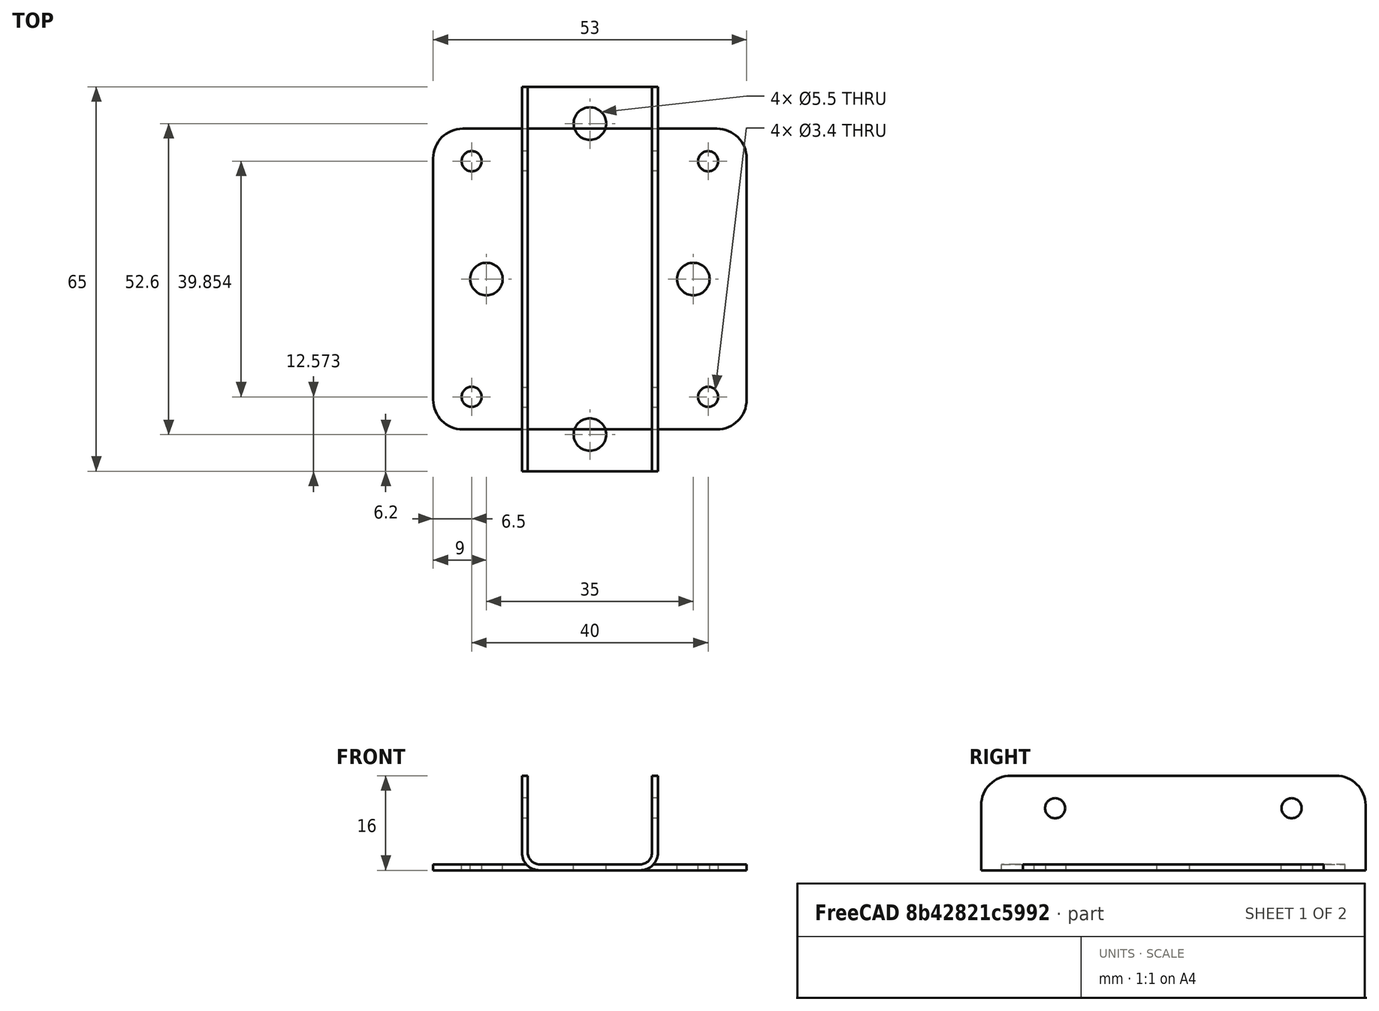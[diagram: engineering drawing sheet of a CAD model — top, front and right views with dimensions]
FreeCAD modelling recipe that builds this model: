
FCSTD DOCUMENT  (FreeCAD 1.1R38827 (Git))
Label: U-fix
License: All rights reserved
LicenseURL: http://en.wikipedia.org/wiki/All_rights_reserved
objects: Sketcher::SketchObject×7, TechDraw::DrawViewDimension×4, TechDraw::DrawViewPart×3, PartDesign::SubShapeBinder×2, PartDesign::Pocket×2, PartDesign::FeaturePython×1, PartDesign::Mirrored×1, TechDraw::DrawSVGTemplate×1, Part::Feature×1, PartDesign::Hole×1, PartDesign::Body×1, TechDraw::DrawPage×1, App::DocumentObjectGroup×1
note: 37 computed .brp shape members not serialized (recipe doc carries the construction recipe); baked Part::Feature solids carry a one-line shape summary decoded from their .brp
EXTERNAL_REF file=ugol90degX40mm.FCStd obj=Binder002
EXTERNAL_REF file=wheel50mm.FCStd obj=Populate001

FEATURE [Sketcher::SketchObject] Sketch
  ArcFitTolerance = 0
  AttachmentSupport = -> [XZ_Plane]
  FullyConstrained = true
  MakeInternals = false
  MapMode = 5
  Placement = pos=(0,0,0) rot=(1,0,0;1.5708rad)
  sketch-geometry (5):
    g0: LineSegment StartX=-11.5 StartY=16 StartZ=0 EndX=-11.5 EndY=0 EndZ=0
    g1: LineSegment StartX=-11.5 StartY=0 StartZ=0 EndX=11.5 EndY=0 EndZ=0
    g2: LineSegment StartX=11.5 StartY=0 StartZ=0 EndX=11.5 EndY=16 EndZ=0
    g3: LineSegment [constr] StartX=11.5 StartY=16 StartZ=0 EndX=-11.5 EndY=16 EndZ=0
    g4: GeomPoint [constr] X=0 Y=8 Z=0
  constraints (13):
    c: Coincident(g0,g1)
    c: Coincident(g1,g2)
    c: Coincident(g2,g3)
    c: Coincident(g3,g0)
    c: Horizontal(g1)
    c: Horizontal(g3)
    c: Vertical(g0)
    c: Vertical(g2)
    c: Symmetric(g1,g0,g4)
    c: PointOnObject(g4,g-2)
    c: PointOnObject(g1,g-1)
    c: DistanceX(g1,g1) = 23  'width'
    c: DistanceY(g2) = 16  'height'
FEATURE [PartDesign::FeaturePython] BaseBend  # WARN: FeaturePython — macro-defined, semantics opaque (R4)
  BendSide = 1
  BendSketch = -> Sketch
  MidPlane = true
  Reverse = false
  Suppressed = false
  length = 65
  radius = 2
  thickness = 1
FEATURE [PartDesign::SubShapeBinder] Binder  label="U-fix_vert_holes"
  BindCopyOnChange = 0
  BindMode = 0
  ClaimChildren = false
  Context = -> Body [Binder.]
  Fuse = false
  MakeFace = true
  OffsetFill = false
  OffsetIntersection = false
  OffsetJoinType = 0
  OffsetOpenResult = false
  PartialLoad = false
  Placement = pos=(0,0,0) rot=(0,0,1;1.5708rad)
  Relative = true
  Support = -> [<external ugol90degX40mm.FCStd>#Binder002]
  _Version = 2
  expr: Support = <<ugol90degX40mm>>#<<vert>>._self
FEATURE [PartDesign::Pocket] Pocket
  BaseFeature = -> BaseBend
  Direction = (1,-2e-16,0)
  Length = 5
  Length2 = 5
  Midplane = true
  Profile = -> Binder
  Suppressed = false
  Type = 1
FEATURE [Sketcher::SketchObject] Sketch001
  ArcFitTolerance = 0
  AttachmentOffset = pos=(32.5,16,0) rot=(0,0,1;0rad)
  AttachmentSupport = -> [YZ_Plane]
  FullyConstrained = true
  MakeInternals = false
  MapMode = 5
  Placement = pos=(0,32.5,16) rot=(0.57735,0.57735,0.57735;2.0944rad)
  expr: .AttachmentOffset.Base.x = BaseBend.length / 2
  expr: .AttachmentOffset.Base.y = Sketch.Constraints.height
  sketch-geometry (3):
    g0: ArcOfCircle CenterX=-5 CenterY=-5 CenterZ=0 NormalX=0 NormalY=0 NormalZ=1 AngleXU=0 Radius=5 StartAngle=0 EndAngle=1.5708
    g1: LineSegment StartX=-9e-16 StartY=-5 StartZ=0 EndX=0 EndY=0 EndZ=0
    g2: LineSegment StartX=0 StartY=0 StartZ=0 EndX=-5.00003 EndY=-4.65468e-11 EndZ=0
  constraints (8):
    c: PointOnObject(g0,g-1)
    c: PointOnObject(g0,g-2)
    c: Coincident(g1,g2)
    c: Coincident(g2,g0)
    c: Tangent(g2,g0)
    c: Tangent(g0,g1) = -1.5708
    c: Coincident(g1,g-1)
    c: Diameter(g0) = 10
FEATURE [PartDesign::Pocket] Pocket001
  BaseFeature = -> Pocket
  Direction = (-1,0,0)
  Length = 5
  Length2 = 5
  Midplane = true
  Profile = -> Sketch001
  ReferenceAxis = -> Sketch001 [N_Axis]
  Suppressed = false
  Type = 1
FEATURE [PartDesign::Mirrored] Mirrored
  BaseFeature = -> Pocket001
  MirrorPlane = -> XZ_Plane
  Originals = -> [Pocket001]
  Suppressed = false
  TransformMode = 0
FEATURE [Sketcher::SketchObject] Sketch002  label="holes_bottom"
  ArcFitTolerance = 0
  AttachmentSupport = -> [XY_Plane]
  FullyConstrained = true
  MakeInternals = false
  MapMode = 5
  sketch-geometry (2):
    g0: Circle CenterX=0 CenterY=17.5 CenterZ=0 NormalX=0 NormalY=0 NormalZ=1 AngleXU=0 Radius=2.5
    g1: Circle CenterX=0 CenterY=-17.5 CenterZ=0 NormalX=0 NormalY=0 NormalZ=1 AngleXU=0 Radius=2.5
  constraints (5):
    c: PointOnObject(g0,g-2)
    c: Symmetric(g1,g0,g-1)
    c: Equal(g1,g0)
    c: Diameter(g1) = 5
    c: DistanceY(g1,g0) = 35
FEATURE [TechDraw::DrawSVGTemplate] Template
  Height = 210
  Orientation = 1
  Template = <path>
  Width = 297
FEATURE [Part::Feature] Unfold
  Placement = pos=(0,0,0) rot=(0,0,1;1.5708rad)
  shape: bbox 53 x 50.85 x 1 mm, 16 faces (baked)
FEATURE [Sketcher::SketchObject] Unfold_Sketch_Outline
  ArcFitTolerance = 0
  FullyConstrained = false
  MakeInternals = false
  sketch-geometry (8):
    g0: ArcOfCircle CenterX=21.5 CenterY=-20.427 CenterZ=0 NormalX=0 NormalY=0 NormalZ=1 AngleXU=4e-16 Radius=5 StartAngle=4.71238 EndAngle=6.28319
    g1: LineSegment StartX=26.5 StartY=20.427 StartZ=0 EndX=26.5 EndY=-20.427 EndZ=0
    g2: ArcOfCircle CenterX=21.5 CenterY=20.427 CenterZ=0 NormalX=0 NormalY=0 NormalZ=1 AngleXU=-4e-16 Radius=5 StartAngle=0 EndAngle=1.5708
    g3: LineSegment StartX=21.5 StartY=25.427 StartZ=0 EndX=-21.5 EndY=25.427 EndZ=0
    g4: ArcOfCircle CenterX=-21.5 CenterY=20.427 CenterZ=0 NormalX=0 NormalY=0 NormalZ=1 AngleXU=-3.14159 Radius=5 StartAngle=4.71238 EndAngle=6.28319
    g5: LineSegment StartX=-26.5 StartY=20.427 StartZ=0 EndX=-26.5 EndY=-20.427 EndZ=0
    g6: ArcOfCircle CenterX=-21.5 CenterY=-20.427 CenterZ=0 NormalX=0 NormalY=0 NormalZ=1 AngleXU=3.14159 Radius=5 StartAngle=0 EndAngle=1.5708
    g7: LineSegment StartX=21.5 StartY=-25.427 StartZ=0 EndX=-21.5 EndY=-25.427 EndZ=0
FEATURE [Sketcher::SketchObject] Unfold_Sketch_Internal
  ArcFitTolerance = 0
  FullyConstrained = false
  MakeInternals = false
  sketch-geometry (6):
    g0: Circle CenterX=17.5 CenterY=0 CenterZ=0 NormalX=0 NormalY=0 NormalZ=1 AngleXU=1.5708 Radius=2.75
    g1: Circle CenterX=-17.5 CenterY=0 CenterZ=0 NormalX=0 NormalY=0 NormalZ=1 AngleXU=1.5708 Radius=2.75
    g2: Circle CenterX=20 CenterY=-19.927 CenterZ=0 NormalX=0 NormalY=0 NormalZ=1 AngleXU=2e-16 Radius=1.7
    g3: Circle CenterX=-20 CenterY=-19.927 CenterZ=0 NormalX=0 NormalY=0 NormalZ=1 AngleXU=2e-16 Radius=1.7
    g4: Circle CenterX=20 CenterY=19.927 CenterZ=0 NormalX=0 NormalY=0 NormalZ=-1 AngleXU=-3.14159 Radius=1.7
    g5: Circle CenterX=-20 CenterY=19.927 CenterZ=0 NormalX=0 NormalY=0 NormalZ=-1 AngleXU=-3.14159 Radius=1.7
FEATURE [Sketcher::SketchObject] Unfold_Sketch_bends
  ArcFitTolerance = 0
  FullyConstrained = false
  MakeInternals = false
  sketch-geometry (2):
    g0: LineSegment StartX=-26.5 StartY=10.4635 StartZ=0 EndX=26.5 EndY=10.4635 EndZ=0
    g1: LineSegment StartX=-26.5 StartY=-10.4635 StartZ=0 EndX=26.5 EndY=-10.4635 EndZ=0
FEATURE [Sketcher::SketchObject] Unfold_Sketch
  ArcFitTolerance = 0
  ExternalGeometry = -> [Unfold_Sketch_bends]
  FullyConstrained = false
  MakeInternals = false
  sketch-geometry (18):
    g0: ArcOfCircle CenterX=21.5 CenterY=-20.427 CenterZ=0 NormalX=0 NormalY=0 NormalZ=1 AngleXU=4e-16 Radius=5 StartAngle=4.71238 EndAngle=6.28319
    g1: LineSegment StartX=21.5 StartY=-25.427 StartZ=0 EndX=-21.5 EndY=-25.427 EndZ=0
    g2: ArcOfCircle CenterX=-21.5 CenterY=-20.427 CenterZ=0 NormalX=0 NormalY=0 NormalZ=1 AngleXU=3.14159 Radius=5 StartAngle=0 EndAngle=1.5708
    g3: ArcOfCircle CenterX=-21.5 CenterY=20.427 CenterZ=0 NormalX=0 NormalY=0 NormalZ=1 AngleXU=-3.14159 Radius=5 StartAngle=4.71238 EndAngle=6.28319
    g4: LineSegment StartX=21.5 StartY=25.427 StartZ=0 EndX=-21.5 EndY=25.427 EndZ=0
    g5: ArcOfCircle CenterX=21.5 CenterY=20.427 CenterZ=0 NormalX=0 NormalY=0 NormalZ=1 AngleXU=-4e-16 Radius=5 StartAngle=0 EndAngle=1.5708
    g6: Circle CenterX=-17.5 CenterY=0 CenterZ=0 NormalX=0 NormalY=0 NormalZ=1 AngleXU=1.5708 Radius=2.75
    g7: Circle CenterX=17.5 CenterY=0 CenterZ=0 NormalX=0 NormalY=0 NormalZ=1 AngleXU=1.5708 Radius=2.75
    g8: Circle CenterX=-20 CenterY=19.927 CenterZ=0 NormalX=0 NormalY=0 NormalZ=-1 AngleXU=-3.14159 Radius=1.7
    g9: Circle CenterX=20 CenterY=19.927 CenterZ=0 NormalX=0 NormalY=0 NormalZ=-1 AngleXU=-3.14159 Radius=1.7
    g10: Circle CenterX=-20 CenterY=-19.927 CenterZ=0 NormalX=0 NormalY=0 NormalZ=1 AngleXU=2e-16 Radius=1.7
    g11: Circle CenterX=20 CenterY=-19.927 CenterZ=0 NormalX=0 NormalY=0 NormalZ=1 AngleXU=2e-16 Radius=1.7
    g12: LineSegment StartX=26.5 StartY=20.427 StartZ=0 EndX=26.5 EndY=-20.427 EndZ=0
    g13: LineSegment StartX=-26.5 StartY=20.427 StartZ=0 EndX=-26.5 EndY=-20.427 EndZ=0
    g14: LineSegment StartX=26.5 StartY=-10.4635 StartZ=0 EndX=24.5 EndY=-10.4635 EndZ=0
    g15: LineSegment StartX=26.5 StartY=10.4635 StartZ=0 EndX=24.5 EndY=10.4635 EndZ=0
    g16: LineSegment StartX=-26.5 StartY=10.4635 StartZ=0 EndX=-24.5 EndY=10.4635 EndZ=0
    g17: LineSegment StartX=-26.5 StartY=-10.4635 StartZ=0 EndX=-24.5 EndY=-10.4635 EndZ=0
  constraints (20):
    c: Coincident(g2,g13)
    c: Coincident(g3,g13)
    c: Coincident(g1,g2)
    c: Coincident(g3,g4)
    c: Coincident(g0,g1)
    c: Coincident(g4,g5)
    c: Coincident(g0,g12)
    c: Coincident(g5,g12)
    c: Coincident(g14,g-4)
    c: Coincident(g15,g-3)
    c: Coincident(g16,g-3)
    c: Coincident(g17,g-4)
    c: PointOnObject(g17,g-4)
    c: PointOnObject(g16,g-3)
    c: PointOnObject(g15,g-3)
    c: PointOnObject(g14,g-4)
    c: Equal(g14,g15)
    c: Equal(g15,g16)
    c: Equal(g16,g17)
    c: Distance(g17) = 2
FEATURE [PartDesign::SubShapeBinder] Binder001
  BindCopyOnChange = 0
  BindMode = 0
  ClaimChildren = false
  Context = -> Body [Binder001.]
  Fuse = false
  MakeFace = true
  OffsetFill = false
  OffsetIntersection = false
  OffsetJoinType = 0
  OffsetOpenResult = false
  PartialLoad = false
  Placement = pos=(0,0,0) rot=(0,0,1;0.785398rad)
  Relative = true
  Support = -> [<external wheel50mm.FCStd>#Populate001]
  _Version = 2
  expr: Support = wheel50mm#<<holes_max>>._self
FEATURE [PartDesign::Hole] Hole
  BaseFeature = -> Mirrored
  CustomThreadClearance = 0
  Depth = 25
  DepthType = 0
  Diameter = 5.5
  DrillForDepth = false
  DrillPoint = 1
  DrillPointAngle = 118
  HoleCutCountersinkAngle = 90
  HoleCutCustomValues = false
  HoleCutDepth = 0
  HoleCutDiameter = 6.1
  HoleCutType = 0
  ModelThread = false
  Profile = -> Binder001
  Reversed = true
  Suppressed = false
  Tapered = false
  TaperedAngle = 90
  ThreadClass = 0
  ThreadDepth = 25
  ThreadDepthType = 0
  ThreadDirection = 0
  ThreadFit = 0
  ThreadSize = 0
  ThreadType = 0
  Threaded = false
  UseCustomThreadClearance = false
FEATURE [PartDesign::Body] Body  label="U_fix_material_0.50ansi"
  AllowCompound = false
  Group = -> [Sketch,BaseBend,Binder,Pocket,Sketch001,Pocket001,Mirrored,Sketch002,Hole,Binder001]
  Origin = -> Origin
  Tip = -> Hole
FEATURE [TechDraw::DrawViewPart] View
  CoarseView = false
  Direction = (0,-1,0)
  Focus = 100
  HardHidden = false
  IsoCount = 0
  IsoHidden = false
  IsoVisible = false
  LockPosition = false
  Perspective = false
  Rotation = 0
  ScaleType = 0
  ScrubCount = 0
  SeamHidden = false
  SeamVisible = true
  SmoothHidden = false
  SmoothVisible = true
  Source = -> [Body]
  X = 69.5
  XDirection = (1,0,0)
  Y = 105
  expr: Y = Template.Height / 2
FEATURE [TechDraw::DrawViewPart] View001
  CoarseView = false
  Direction = (1,0,0)
  Focus = 100
  HardHidden = false
  IsoCount = 0
  IsoHidden = false
  IsoVisible = false
  LockPosition = false
  Perspective = false
  Rotation = 0
  ScaleType = 0
  ScrubCount = 0
  SeamHidden = false
  SeamVisible = true
  SmoothHidden = false
  SmoothVisible = true
  Source = -> [Body]
  X = 226.5
  XDirection = (0,1,-1.19209e-07)
  Y = 105
  expr: Y = Template.Height / 2
FEATURE [TechDraw::DrawViewPart] View002
  CoarseView = false
  Direction = (0,0,1)
  Focus = 100
  HardHidden = false
  IsoCount = 0
  IsoHidden = false
  IsoVisible = false
  LockPosition = false
  Perspective = false
  Rotation = 0
  ScaleType = 0
  ScrubCount = 0
  SeamHidden = false
  SeamVisible = true
  SmoothHidden = false
  SmoothVisible = true
  Source = -> [Body]
  X = 148.5
  XDirection = (1,0,0)
  Y = 105
  expr: Y = Template.Height / 2
FEATURE [TechDraw::DrawViewDimension] Dimension004
  AngleOverride = false
  Arbitrary = false
  ArbitraryTolerances = false
  EqualTolerance = true
  ExtensionAngle = 0
  FormatSpec = R%.2w
  FormatSpecOverTolerance = %+.2w
  FormatSpecUnderTolerance = %+.2w
  Inverted = false
  LineAngle = 0
  LockPosition = false
  MeasureType = 1
  OverTolerance = 0
  References2D = -> [View]
  Rotation = 0
  ScaleType = 0
  TheoreticalExact = false
  Type = 4
  UnderTolerance = 0
  X = -23.1952
  Y = -5.48414
FEATURE [TechDraw::DrawViewDimension] Dimension005
  AngleOverride = false
  Arbitrary = false
  ArbitraryTolerances = false
  EqualTolerance = true
  ExtensionAngle = 0
  FormatSpec = R%.2w
  FormatSpecOverTolerance = %+.2w
  FormatSpecUnderTolerance = %+.2w
  Inverted = false
  LineAngle = 0
  LockPosition = false
  MeasureType = 1
  OverTolerance = 0
  References2D = -> [View]
  Rotation = 0
  ScaleType = 0
  TheoreticalExact = false
  Type = 4
  UnderTolerance = 0
  X = 1.1181
  Y = 3.75976
FEATURE [TechDraw::DrawViewDimension] Dimension
  AngleOverride = false
  Arbitrary = false
  ArbitraryTolerances = false
  BoxCorners = (2) [(-11.5,-8,-1e-07),(11.5,8,1e-07)]
  EqualTolerance = true
  ExtensionAngle = 0
  FormatSpec = %.2w
  FormatSpecOverTolerance = %+.2w
  FormatSpecUnderTolerance = %+.2w
  Inverted = false
  LineAngle = 0
  LockPosition = false
  MeasureType = 1
  OverTolerance = 0
  References2D = -> [View]
  Rotation = 0
  ScaleType = 0
  TheoreticalExact = false
  Type = 1
  UnderTolerance = 0
  X = -0.401552
  Y = 25.4578
FEATURE [TechDraw::DrawViewDimension] Dimension006
  AngleOverride = false
  Arbitrary = false
  ArbitraryTolerances = false
  BoxCorners = (2) [(-11.5,-8,-1e-07),(11.5,8,1e-07)]
  EqualTolerance = true
  ExtensionAngle = 0
  FormatSpec = %.2w
  FormatSpecOverTolerance = %+.2w
  FormatSpecUnderTolerance = %+.2w
  Inverted = false
  LineAngle = 0
  LockPosition = false
  MeasureType = 1
  OverTolerance = 0
  References2D = -> [View]
  Rotation = 0
  ScaleType = 0
  TheoreticalExact = false
  Type = 2
  UnderTolerance = 0
  X = 18.6275
  Y = 2.60039
FEATURE [TechDraw::DrawPage] Page
  KeepUpdated = true
  NextBalloonIndex = 1
  ProjectionType = 0
  Template = -> Template
  Views = -> [View,View001,View002,Dimension004,Dimension005,Dimension,Dimension006]
FEATURE [App::DocumentObjectGroup] Group  label="unfold_Group"
  Group = -> [Page,Unfold,Unfold_Sketch,Unfold_Sketch_Outline,Unfold_Sketch_Internal,Unfold_Sketch_bends]
note: 1 file-system path scrubbed to <path> (originals preserved in the JSON sidecar)
